# Revit family: Toilet_Paper_Holder-American_Standard-Glenmere-7617230_Series
name_source: partatom
category: Specialty Equipment
units: mm (PartAtom-declared; Revit-internal decimal feet)

## family parameters
Cut with Voids When Loaded = No
Host = Face
OmniClass Number = 23.40.20.21
OmniClass Title = Toilet and Bath Specialties
Part Type = Normal
Room Calculation Point = No
Round Connector Dimension = Use Diameter
Shared = Yes

## types (4) — shared parameters
Assembly Code = C1030220
Default Elevation = 40"
Description = Glenmere Toilet Paper Holder
Installation Type = Wall Mounted
Manufacturer = American Standard
Product Page URL = https://www.americanstandard-us.com
URL = http://www.americanstandard-us.com

## per-type parameters (varying)
| type | Finish | Material |
| 7617230.002 | Metal-American Standard-002-Polished Chrome | Metal-American Standard-002-Polished Chrome |
| 7617230.243 | Metal-American Standard-243-Matte Black | Metal-American Standard-243-Matte Black |
| 7617230.278 | Metal-American Standard-278-Legacy Bronze | Metal-American Standard-278-Legacy Bronze |
| 7617230.295 | Metal-American Standard-295-Brushed Nickel | Metal-American Standard-295-Brushed Nickel |

note: column(s) folded — value = type name in every type: Model

## geometry (parser evidence)
native form markers: Sweep x3
no freeform markers — native parametric forms only
